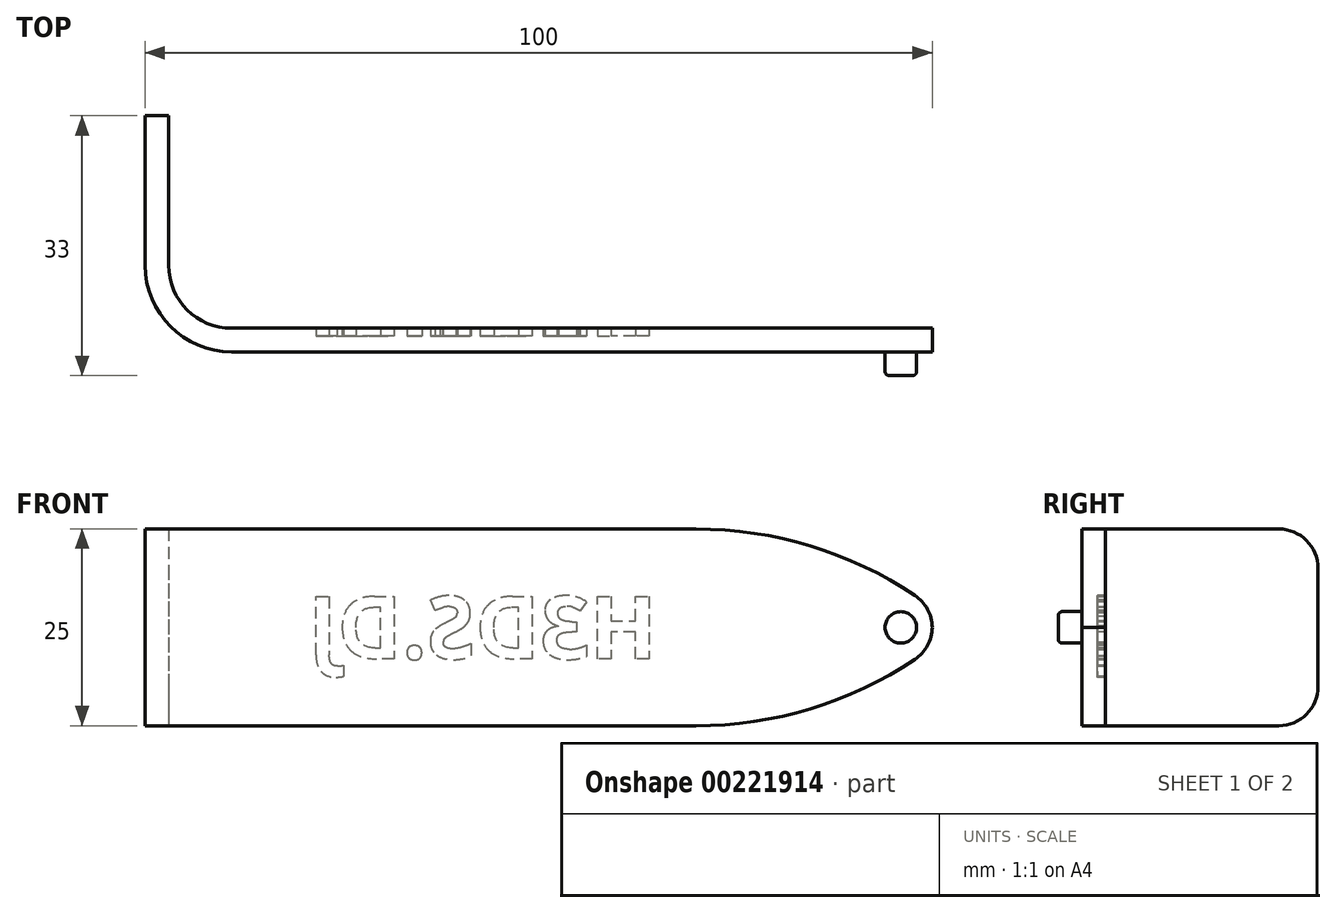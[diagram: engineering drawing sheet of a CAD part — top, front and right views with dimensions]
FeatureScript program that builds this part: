
annotation { "Feature Type Name" : "Feature", "Feature Type Description" : "" }
export const myFeature = defineFeature(function(context is Context, id is Id, definition is map)
    precondition{}
    {
        {
            var Q0;
            Q0=qCreatedBy(makeId("Top.planeOp"),FACE);
            var sketch = newSketch(context, id + "F0", { "sketchPlane" : qUnion([Q0])});
            skLineSegment(sketch, "E0.bottom", {"start": v(11, 0) * mm, "end": v(100, 0) * mm});
            skLineSegment(sketch, "E0.top", {"start": v(11, 3) * mm, "end": v(100, 3) * mm});
            skLineSegment(sketch, "E0.right", {"start": v(100, 0) * mm, "end": v(100, 3) * mm});
            skLineSegment(sketch, "E1.top", {"start": v(0, 30) * mm, "end": v(3, 30) * mm});
            skLineSegment(sketch, "E1.left", {"start": v(0, 11) * mm, "end": v(0, 30) * mm});
            skLineSegment(sketch, "E1.right", {"start": v(3, 11) * mm, "end": v(3, 30) * mm});
            skPoint(sketch, "E2.visualSharp", {"position": v(3, 3) * mm});
            skArc(sketch, "E2.filletArc", {"start": v(3, 11) * mm, "mid": v(5.34, 5.34) * mm, "end": v(11, 3) * mm});
            skArc(sketch, "E3.0", {"start": v(0, 11) * mm, "mid": v(3.22, 3.22) * mm, "end": v(11, 0) * mm});
            skSolve(sketch);
        }
        {
            var Q0;
            Q0=makeQuery(id+"F0.imprint","IMPRINT",FACE,{"disambiguationData":[TD([[makeQuery(id+"F0.imprint","IMPRINT",EDGE,{"derivedFrom":sQuery(id+"F0.wireOp",EDGE,"E0.bottom")}),1.0]])]});
            extrude(context, id + "F1", {"entities" : qUnion([Q0]), "depth" : 25 * mm});
        }
        {
            var Q0;
            Q0=makeQuery(id+"F1.opExtrude","SWEPT_FACE",FACE,{"disambiguationData":[OSD([sQuery(id+"F0.wireOp",EDGE,"E0.bottom")])]});
            var sketch = newSketch(context, id + "F2", { "sketchPlane" : qUnion([Q0])});
            skCircle(sketch, "E4", {"center": v(96, 12.5) * mm, "radius": 2 * mm});
            skSolve(sketch);
        }
        {
            var Q0;
            Q0 = qSketchRegion(id + "F2", true);
            extrude(context, id + "F3", {"entities" : qUnion([Q0]), "operationType" : NewBodyOperationType.ADD, "depth" : 3 * mm});
        }
        {
            var Q0;
            Q0=makeQuery(id+"F1.opExtrude","CAP_EDGE",EDGE,{"disambiguationData":[OSD([sQuery(id+"F0.wireOp",EDGE,"E0.right")])],"isStart":false});
            var Q1;
            Q1=makeQuery(id+"F1.opExtrude","CAP_EDGE",EDGE,{"disambiguationData":[OSD([sQuery(id+"F0.wireOp",EDGE,"E0.right")])],"isStart":true});
            chamfer(context, id + "F4", {"entities" : qUnion([Q0, Q1]), "width" : 10 * mm, "tangentPropagation" : true});
        }
        {
            var Q0;
            {var subQ0=sQuery(id+"F0.wireOp",EDGE,"E0.right");Q0=makeQuery(id+"F4.opChamfer","BLEND_EDGE",EDGE,{"blendedFrom":[makeQuery(id+"F1.opExtrude","CAP_EDGE",EDGE,{"disambiguationData":[OSD([subQ0])],"isStart":false}),makeQuery(id+"F1.opExtrude","CAP_FACE",FACE,{"disambiguationData":[OSD([sQuery(id+"F0.wireOp",EDGE,"E0.bottom"),sQuery(id+"F0.wireOp",EDGE,"E0.top"),subQ0,sQuery(id+"F0.wireOp",EDGE,"E1.top"),sQuery(id+"F0.wireOp",EDGE,"E1.left"),sQuery(id+"F0.wireOp",EDGE,"E1.right"),sQuery(id+"F0.wireOp",EDGE,"E2.filletArc"),sQuery(id+"F0.wireOp",EDGE,"E3.0")])],"isStart":false})],"blendedInto":[makeQuery(id+"F1.opExtrude","CAP_FACE",FACE,{"disambiguationData":[OSD([sQuery(id+"F0.wireOp",EDGE,"E0.bottom"),sQuery(id+"F0.wireOp",EDGE,"E0.top"),subQ0,sQuery(id+"F0.wireOp",EDGE,"E1.top"),sQuery(id+"F0.wireOp",EDGE,"E1.left"),sQuery(id+"F0.wireOp",EDGE,"E1.right"),sQuery(id+"F0.wireOp",EDGE,"E2.filletArc"),sQuery(id+"F0.wireOp",EDGE,"E3.0")])],"isStart":false})]});}
            var Q1;
            {var subQ0=sQuery(id+"F0.wireOp",EDGE,"E0.right");Q1=makeQuery(id+"F4.opChamfer","BLEND_EDGE",EDGE,{"blendedFrom":[makeQuery(id+"F1.opExtrude","CAP_EDGE",EDGE,{"disambiguationData":[OSD([subQ0])],"isStart":true}),makeQuery(id+"F1.opExtrude","CAP_FACE",FACE,{"disambiguationData":[OSD([sQuery(id+"F0.wireOp",EDGE,"E0.bottom"),sQuery(id+"F0.wireOp",EDGE,"E0.top"),subQ0,sQuery(id+"F0.wireOp",EDGE,"E1.top"),sQuery(id+"F0.wireOp",EDGE,"E1.left"),sQuery(id+"F0.wireOp",EDGE,"E1.right"),sQuery(id+"F0.wireOp",EDGE,"E2.filletArc"),sQuery(id+"F0.wireOp",EDGE,"E3.0")])],"isStart":true})],"blendedInto":[makeQuery(id+"F1.opExtrude","CAP_FACE",FACE,{"disambiguationData":[OSD([sQuery(id+"F0.wireOp",EDGE,"E0.bottom"),sQuery(id+"F0.wireOp",EDGE,"E0.top"),subQ0,sQuery(id+"F0.wireOp",EDGE,"E1.top"),sQuery(id+"F0.wireOp",EDGE,"E1.left"),sQuery(id+"F0.wireOp",EDGE,"E1.right"),sQuery(id+"F0.wireOp",EDGE,"E2.filletArc"),sQuery(id+"F0.wireOp",EDGE,"E3.0")])],"isStart":true})]});}
            fillet(context, id + "F5", {"entities" : qUnion([Q0, Q1]), "radius" : 50 * mm, "tangentPropagation" : true, "allowEdgeOverflow" : false});
        }
        {
            var Q0;
            {var subQ0=sQuery(id+"F0.wireOp",EDGE,"E0.right");Q0=makeQuery(id+"F5.opFillet","BLEND_EDGE",EDGE,{"blendedFrom":[makeQuery(id+"F4.opChamfer","BLEND_EDGE",EDGE,{"blendedFrom":[makeQuery(id+"F1.opExtrude","CAP_EDGE",EDGE,{"disambiguationData":[OSD([subQ0])],"isStart":false}),makeQuery(id+"F1.opExtrude","CAP_FACE",FACE,{"disambiguationData":[OSD([sQuery(id+"F0.wireOp",EDGE,"E0.bottom"),sQuery(id+"F0.wireOp",EDGE,"E0.top"),subQ0,sQuery(id+"F0.wireOp",EDGE,"E1.top"),sQuery(id+"F0.wireOp",EDGE,"E1.left"),sQuery(id+"F0.wireOp",EDGE,"E1.right"),sQuery(id+"F0.wireOp",EDGE,"E2.filletArc"),sQuery(id+"F0.wireOp",EDGE,"E3.0")])],"isStart":false})],"blendedInto":[makeQuery(id+"F1.opExtrude","CAP_FACE",FACE,{"disambiguationData":[OSD([sQuery(id+"F0.wireOp",EDGE,"E0.bottom"),sQuery(id+"F0.wireOp",EDGE,"E0.top"),subQ0,sQuery(id+"F0.wireOp",EDGE,"E1.top"),sQuery(id+"F0.wireOp",EDGE,"E1.left"),sQuery(id+"F0.wireOp",EDGE,"E1.right"),sQuery(id+"F0.wireOp",EDGE,"E2.filletArc"),sQuery(id+"F0.wireOp",EDGE,"E3.0")])],"isStart":false})]}),makeQuery(id+"F1.opExtrude","SWEPT_FACE",FACE,{"disambiguationData":[OSD([subQ0])]})],"blendedInto":[makeQuery(id+"F1.opExtrude","SWEPT_FACE",FACE,{"disambiguationData":[OSD([subQ0])]})]});}
            var Q1;
            {var subQ0=sQuery(id+"F0.wireOp",EDGE,"E0.right");Q1=makeQuery(id+"F5.opFillet","BLEND_EDGE",EDGE,{"blendedFrom":[makeQuery(id+"F4.opChamfer","BLEND_EDGE",EDGE,{"blendedFrom":[makeQuery(id+"F1.opExtrude","CAP_EDGE",EDGE,{"disambiguationData":[OSD([subQ0])],"isStart":true}),makeQuery(id+"F1.opExtrude","CAP_FACE",FACE,{"disambiguationData":[OSD([sQuery(id+"F0.wireOp",EDGE,"E0.bottom"),sQuery(id+"F0.wireOp",EDGE,"E0.top"),subQ0,sQuery(id+"F0.wireOp",EDGE,"E1.top"),sQuery(id+"F0.wireOp",EDGE,"E1.left"),sQuery(id+"F0.wireOp",EDGE,"E1.right"),sQuery(id+"F0.wireOp",EDGE,"E2.filletArc"),sQuery(id+"F0.wireOp",EDGE,"E3.0")])],"isStart":true})],"blendedInto":[makeQuery(id+"F1.opExtrude","CAP_FACE",FACE,{"disambiguationData":[OSD([sQuery(id+"F0.wireOp",EDGE,"E0.bottom"),sQuery(id+"F0.wireOp",EDGE,"E0.top"),subQ0,sQuery(id+"F0.wireOp",EDGE,"E1.top"),sQuery(id+"F0.wireOp",EDGE,"E1.left"),sQuery(id+"F0.wireOp",EDGE,"E1.right"),sQuery(id+"F0.wireOp",EDGE,"E2.filletArc"),sQuery(id+"F0.wireOp",EDGE,"E3.0")])],"isStart":true})]}),makeQuery(id+"F1.opExtrude","SWEPT_FACE",FACE,{"disambiguationData":[OSD([subQ0])]})],"blendedInto":[makeQuery(id+"F1.opExtrude","SWEPT_FACE",FACE,{"disambiguationData":[OSD([subQ0])]})]});}
            fillet(context, id + "F6", {"entities" : qUnion([Q0, Q1]), "radius" : 5 * mm, "tangentPropagation" : true, "allowEdgeOverflow" : false});
        }
        {
            var Q0;
            Q0=makeQuery(id+"F3.opExtrude","CAP_EDGE",EDGE,{"disambiguationData":[OSD([sQuery(id+"F2.wireOp",EDGE,"E4")])],"isStart":true});
            var Q1;
            Q1=makeQuery(id+"F3.opExtrude","CAP_EDGE",EDGE,{"disambiguationData":[OSD([sQuery(id+"F2.wireOp",EDGE,"E4")])],"isStart":false});
            fillet(context, id + "F7", {"entities" : qUnion([Q0, Q1]), "radius" : .5 * mm, "tangentPropagation" : true, "allowEdgeOverflow" : false});
        }
        {
            var Q0;
            Q0=makeQuery(id+"F1.opExtrude","CAP_EDGE",EDGE,{"disambiguationData":[OSD([sQuery(id+"F0.wireOp",EDGE,"E1.top")])],"isStart":false});
            var Q1;
            Q1=makeQuery(id+"F1.opExtrude","CAP_EDGE",EDGE,{"disambiguationData":[OSD([sQuery(id+"F0.wireOp",EDGE,"E1.top")])],"isStart":true});
            fillet(context, id + "F8", {"entities" : qUnion([Q0, Q1]), "radius" : 5 * mm, "tangentPropagation" : true, "allowEdgeOverflow" : false});
        }
        {
            var Q0;
            Q0=makeQuery(id+"F1.opExtrude","SWEPT_FACE",FACE,{"disambiguationData":[OSD([sQuery(id+"F0.wireOp",EDGE,"E0.top")])]});
            var sketch = newSketch(context, id + "F9", { "sketchPlane" : qUnion([Q0])});
            skText(sketch, "E5", { "text": "H3DS.DJ\n", "fontName": "OpenSans-Bold.ttf"});
            const initialGuessF9  = {"E5": [-0.06498, 0.0085, 1, 0, 0.008]};
            skSetInitialGuess(sketch, initialGuessF9);
            skSolve(sketch);
        }
        {
            var Q0;
            Q0 = qSketchRegion(id + "F9", true);
            extrude(context, id + "F10", {"entities" : qUnion([Q0]), "operationType" : NewBodyOperationType.REMOVE, "endBound" : BoundingType.SYMMETRIC, "depth" : 2 * mm});
        }
    });
